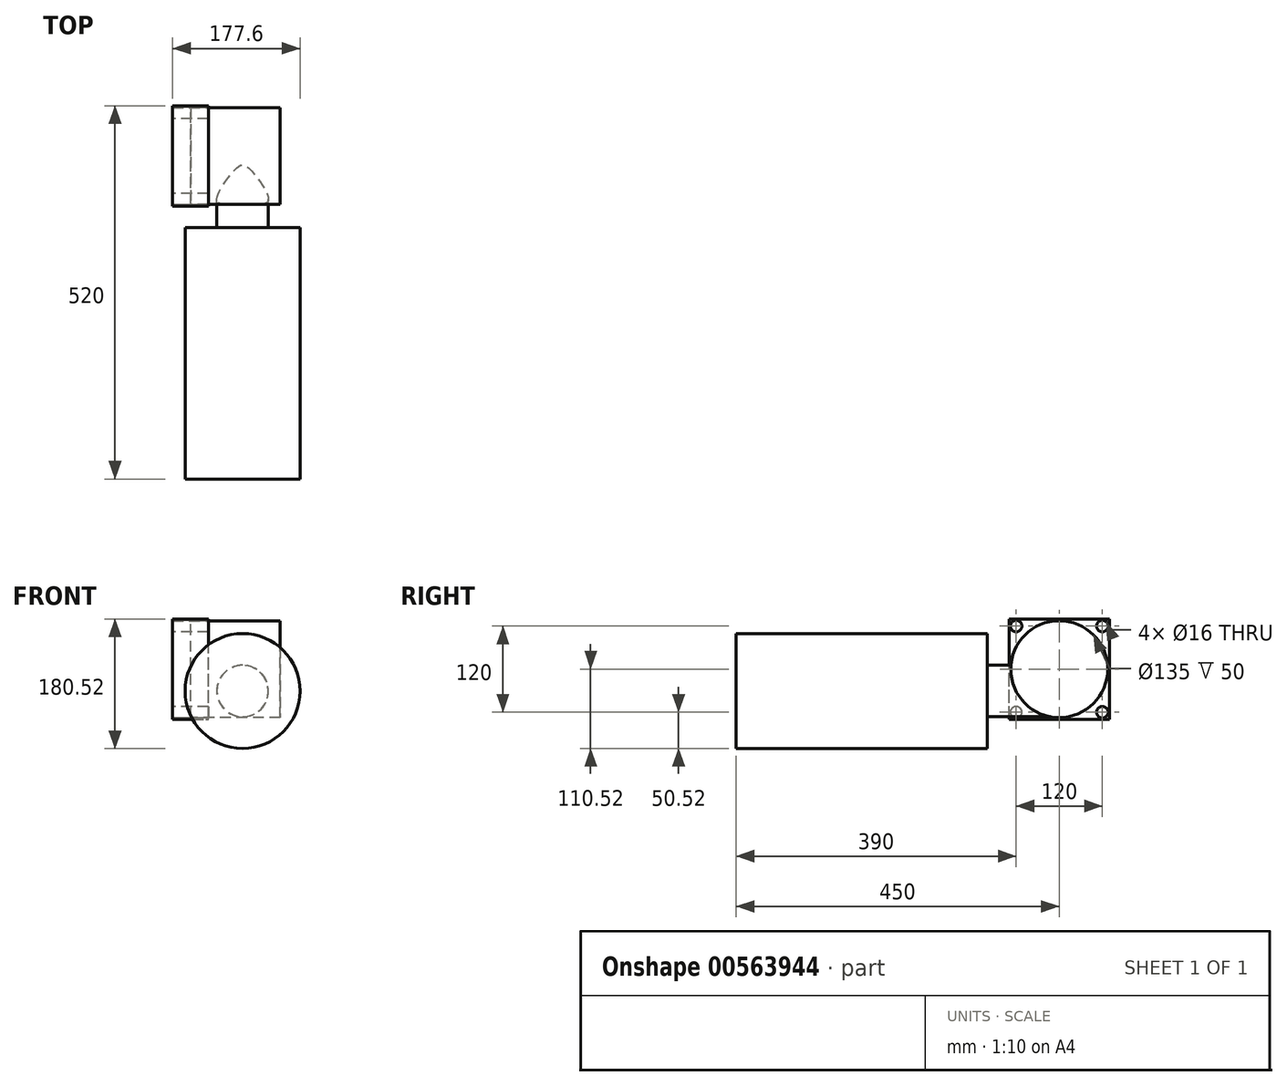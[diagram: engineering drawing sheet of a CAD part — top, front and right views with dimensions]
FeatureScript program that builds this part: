
annotation { "Feature Type Name" : "Feature", "Feature Type Description" : "" }
export const myFeature = defineFeature(function(context is Context, id is Id, definition is map)
    precondition{}
    {
        {
            var Q0;
            Q0=qCreatedBy(makeId("Right.planeOp"),FACE);
            var sketch = newSketch(context, id + "F0", { "sketchPlane" : qUnion([Q0])});
            skCircle(sketch, "E0", {"center": v(0, 0) * mm, "radius": 67.5 * mm});
            skLineSegment(sketch, "E1.bottom", {"start": v(70, -70) * mm, "end": v(-70, -70) * mm});
            skLineSegment(sketch, "E1.top", {"start": v(70, 70) * mm, "end": v(-70, 70) * mm});
            skLineSegment(sketch, "E1.left", {"start": v(70, -70) * mm, "end": v(70, 70) * mm});
            skLineSegment(sketch, "E1.right", {"start": v(-70, -70) * mm, "end": v(-70, 70) * mm});
            skSolve(sketch);
        }
        {
            var Q0;
            {var subQ0=sQuery(id+"F0.wireOp",EDGE,"E1.top");var subQ1=sQuery(id+"F0.wireOp",EDGE,"E0");var subQ2=makeQuery(id+"F0.imprint","INTERSECT",VERTEX,{"derivedFrom":[subQ1,subQ0]});Q0=makeQuery(id+"F0.imprint","IMPRINT",FACE,{"disambiguationData":[TD([[makeQuery(id+"F0.imprint","IMPRINT",EDGE,{"disambiguationData":[TD([[subQ2,-1.0]])],"derivedFrom":subQ1}),-1.0]])]});}
            var Q1;
            {var subQ0=sQuery(id+"F0.wireOp",EDGE,"E1.top");var subQ1=sQuery(id+"F0.wireOp",EDGE,"E0");var subQ2=makeQuery(id+"F0.imprint","INTERSECT",VERTEX,{"derivedFrom":[subQ1,subQ0]});Q1=makeQuery(id+"F0.imprint","IMPRINT",FACE,{"disambiguationData":[TD([[makeQuery(id+"F0.imprint","IMPRINT",EDGE,{"disambiguationData":[TD([[subQ2,1.0]])],"derivedFrom":subQ1}),-1.0]])]});}
            var Q2;
            {var subQ0=sQuery(id+"F0.wireOp",EDGE,"E1.left");var subQ1=sQuery(id+"F0.wireOp",EDGE,"E0");var subQ2=makeQuery(id+"F0.imprint","INTERSECT",VERTEX,{"derivedFrom":[subQ1,subQ0]});Q2=makeQuery(id+"F0.imprint","IMPRINT",FACE,{"disambiguationData":[TD([[makeQuery(id+"F0.imprint","IMPRINT",EDGE,{"disambiguationData":[TD([[subQ2,1.0]])],"derivedFrom":subQ1}),-1.0]])]});}
            var Q3;
            {var subQ0=sQuery(id+"F0.wireOp",EDGE,"E1.right");var subQ1=sQuery(id+"F0.wireOp",EDGE,"E0");var subQ2=makeQuery(id+"F0.imprint","INTERSECT",VERTEX,{"derivedFrom":[subQ1,subQ0]});Q3=makeQuery(id+"F0.imprint","IMPRINT",FACE,{"disambiguationData":[TD([[makeQuery(id+"F0.imprint","IMPRINT",EDGE,{"disambiguationData":[TD([[subQ2,-1.0]])],"derivedFrom":subQ1}),-1.0]])]});}
            extrude(context, id + "F1", {"entities" : qUnion([Q0, Q1, Q2, Q3]), "oppositeDirection" : true, "depth" : 50 * mm, "offsetDistance" : 25 * mm});
        }
        {
            var Q0;
            Q0=makeQuery(id+"F1.opExtrude","CAP_FACE",FACE,{"disambiguationData":[OSD([sQuery(id+"F0.wireOp",EDGE,"E0"),sQuery(id+"F0.wireOp",EDGE,"E1.bottom"),sQuery(id+"F0.wireOp",EDGE,"E1.top"),sQuery(id+"F0.wireOp",EDGE,"E1.left"),sQuery(id+"F0.wireOp",EDGE,"E1.right")])],"isStart":true});
            var sketch = newSketch(context, id + "F2", { "sketchPlane" : qUnion([Q0])});
            skSolve(sketch);
        }
        {
            var Q0;
            Q0=makeQuery(id+"F2.imprint","IMPRINT",FACE,{"disambiguationData":[TD([[makeQuery(id+"F2.imprint","IMPRINT",EDGE,{"derivedFrom":makeQuery(id+"F1.opExtrude","CAP_EDGE",EDGE,{"disambiguationData":[OSD([sQuery(id+"F0.wireOp",EDGE,"E0")])],"isStart":true})}),1.0]])]});
            extrude(context, id + "F3", {"entities" : qUnion([Q0]), "depth" : 100 * mm, "offsetDistance" : 25 * mm, "hasSecondDirection" : true, "secondDirectionOppositeDirection" : true, "secondDirectionDepth" : 25 * mm});
        }
        {
            var Q0;
            Q0=makeQuery(id+"F3.opExtrude","CAP_FACE",FACE,{"disambiguationData":[OSD([sQuery(id+"F0.wireOp",EDGE,"E0")])],"isStart":true});
            var sketch = newSketch(context, id + "F4", { "sketchPlane" : qUnion([Q0])});
            skCircle(sketch, "E2", {"center": v(60, -60) * mm, "radius": 8 * mm});
            skCircle(sketch, "E3", {"center": v(-60, 60) * mm, "radius": 8 * mm});
            skCircle(sketch, "E4", {"center": v(60, 60) * mm, "radius": 8 * mm});
            skCircle(sketch, "E5", {"center": v(-60, -60) * mm, "radius": 8 * mm});
            skSolve(sketch);
        }
        {
            var Q0;
            Q0=makeQuery(id+"F4.imprint","IMPRINT",FACE,{"disambiguationData":[TD([[makeQuery(id+"F4.imprint","IMPRINT",EDGE,{"derivedFrom":sQuery(id+"F4.wireOp",EDGE,"E4")}),1.0]])]});
            var Q1;
            Q1=makeQuery(id+"F4.imprint","IMPRINT",FACE,{"disambiguationData":[TD([[makeQuery(id+"F4.imprint","IMPRINT",EDGE,{"derivedFrom":sQuery(id+"F4.wireOp",EDGE,"E3")}),1.0]])]});
            var Q2;
            Q2=makeQuery(id+"F4.imprint","IMPRINT",FACE,{"disambiguationData":[TD([[makeQuery(id+"F4.imprint","IMPRINT",EDGE,{"derivedFrom":sQuery(id+"F4.wireOp",EDGE,"E5")}),1.0]])]});
            var Q3;
            Q3=makeQuery(id+"F4.imprint","IMPRINT",FACE,{"disambiguationData":[TD([[makeQuery(id+"F4.imprint","IMPRINT",EDGE,{"derivedFrom":sQuery(id+"F4.wireOp",EDGE,"E2")}),1.0]])]});
            extrude(context, id + "F5", {"entities" : qUnion([Q0, Q1, Q2, Q3]), "operationType" : NewBodyOperationType.REMOVE, "endBound" : BoundingType.SYMMETRIC, "oppositeDirection" : true, "depth" : 50 * mm, "offsetDistance" : 25 * mm});
        }
        {
            var Q0;
            Q0=qCreatedBy(makeId("Front.planeOp"),FACE);
            var sketch = newSketch(context, id + "F6", { "sketchPlane" : qUnion([Q0])});
            skCircle(sketch, "E6", {"center": v(47.53, -30.45) * mm, "radius": 35.98 * mm});
            skSolve(sketch);
        }
        {
            var Q0;
            Q0 = qSketchRegion(id + "F6", true);
            extrude(context, id + "F7", {"entities" : qUnion([Q0]), "operationType" : NewBodyOperationType.ADD, "depth" : 100 * mm, "offsetDistance" : 25 * mm});
        }
        {
            var Q0;
            Q0=makeQuery(id+"F7.opExtrude","CAP_FACE",FACE,{"disambiguationData":[OSD([sQuery(id+"F6.wireOp",EDGE,"E6")])],"isStart":false});
            var sketch = newSketch(context, id + "F8", { "sketchPlane" : qUnion([Q0])});
            skCircle(sketch, "E7", {"center": v(47.53, -30.45) * mm, "radius": 80.07 * mm});
            skSolve(sketch);
        }
        {
            var Q0;
            Q0=makeQuery(id+"F8.imprint","IMPRINT",FACE,{"disambiguationData":[TD([[makeQuery(id+"F8.imprint","IMPRINT",EDGE,{"derivedFrom":sQuery(id+"F8.wireOp",EDGE,"E7")}),1.0]])]});
            var Q1;
            Q1=makeQuery(id+"F8.imprint","IMPRINT",FACE,{"disambiguationData":[TD([[makeQuery(id+"F8.imprint","IMPRINT",EDGE,{"derivedFrom":makeQuery(id+"F7.opExtrude","CAP_EDGE",EDGE,{"disambiguationData":[OSD([sQuery(id+"F6.wireOp",EDGE,"E6")])],"isStart":false})}),1.0]])]});
            extrude(context, id + "F9", {"entities" : qUnion([Q0, Q1]), "operationType" : NewBodyOperationType.ADD, "depth" : 350 * mm, "offsetDistance" : 25 * mm});
        }
    });
